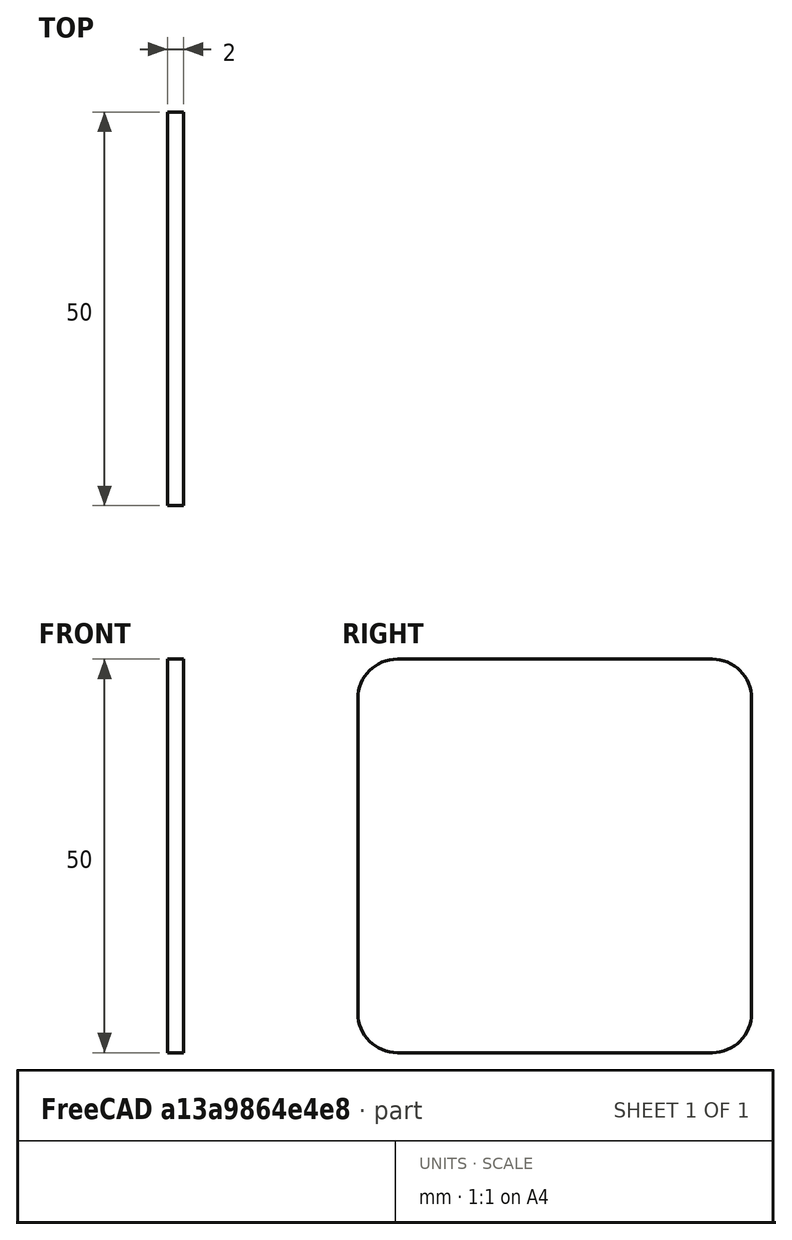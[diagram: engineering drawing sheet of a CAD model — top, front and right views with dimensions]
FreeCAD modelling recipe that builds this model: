
FCSTD DOCUMENT  (FreeCAD 0.20R25352 (Git))
Label: gopro mount
License: All rights reserved
LicenseURL: http://en.wikipedia.org/wiki/All_rights_reserved
objects: Sketcher::SketchObject×2, PartDesign::Pad×1, PartDesign::Body×1
note: 5 computed .brp shape members not serialized (recipe doc carries the construction recipe); baked Part::Feature solids carry a one-line shape summary decoded from their .brp

FEATURE [Sketcher::SketchObject] Sketch003
  FullyConstrained = true
  MapMode = 3
  Placement = pos=(0,0,0) rot=(0.707107,0.707107,0;3.14159rad)
  Support = -> [Sketch003]
  sketch-geometry (5):
    g0: LineSegment StartX=-8 StartY=0 StartZ=0 EndX=8 EndY=0 EndZ=0
    g1: LineSegment StartX=8 StartY=0 StartZ=0 EndX=8 EndY=12 EndZ=0
    g2: LineSegment StartX=-8 StartY=12 StartZ=0 EndX=-8 EndY=0 EndZ=0
    g3: ArcOfCircle CenterX=0 CenterY=12 CenterZ=0 NormalX=0 NormalY=0 NormalZ=1 AngleXU=0 Radius=8 StartAngle=0 EndAngle=3.14159
    g4: Circle CenterX=0 CenterY=12 CenterZ=0 NormalX=0 NormalY=0 NormalZ=1 AngleXU=0 Radius=3
  constraints (14):
    c: Vertical(g2)
    c: Vertical(g1)
    c: Horizontal(g2,g1)
    c: DistanceY(g2,g2) = 12
    c: Coincident(g3,g2)
    c: Coincident(g3,g1)
    c: Coincident(g4,g3)
    c: Diameter(g4) = 6
    c: Horizontal(g0)
    c: Horizontal(g3,g2)
    c: Coincident(g2,g0)
    c: Coincident(g0,g1)
    c: DistanceX(g0,g0) = 16
    c: Symmetric(g0,g0,g-1)
FEATURE [Sketcher::SketchObject] Sketch004
  FullyConstrained = true
  MapMode = 2
  Placement = pos=(-1.65,7e-16,-5e-16) rot=(0.57735,0.57735,-0.57735;4.18879rad)
  Support = -> [Sketch004]
  sketch-geometry (12):
    g0: LineSegment StartX=-20 StartY=25 StartZ=0 EndX=20 EndY=25 EndZ=0
    g1: LineSegment StartX=25 StartY=20 StartZ=0 EndX=25 EndY=-20 EndZ=0
    g2: LineSegment StartX=20 StartY=-25 StartZ=0 EndX=-20 EndY=-25 EndZ=0
    g3: LineSegment StartX=-25 StartY=-20 StartZ=0 EndX=-25 EndY=20 EndZ=0
    g4: ArcOfCircle CenterX=20 CenterY=20 CenterZ=0 NormalX=0 NormalY=0 NormalZ=1 AngleXU=0 Radius=5 StartAngle=0 EndAngle=1.5708
    g5: GeomPoint X=25 Y=25 Z=0
    g6: ArcOfCircle CenterX=20 CenterY=-20 CenterZ=0 NormalX=0 NormalY=0 NormalZ=1 AngleXU=0 Radius=5 StartAngle=4.71239 EndAngle=6.28319
    g7: GeomPoint X=25 Y=-25 Z=0
    g8: ArcOfCircle CenterX=-20 CenterY=-20 CenterZ=0 NormalX=0 NormalY=0 NormalZ=1 AngleXU=0 Radius=5 StartAngle=3.14159 EndAngle=4.71239
    g9: GeomPoint X=-25 Y=-25 Z=0
    g10: ArcOfCircle CenterX=-20 CenterY=20 CenterZ=0 NormalX=0 NormalY=0 NormalZ=1 AngleXU=0 Radius=5 StartAngle=1.5708 EndAngle=3.14159
    g11: GeomPoint X=-25 Y=25 Z=0
  constraints (26):
    c: Horizontal(g2)
    c: Vertical(g1)
    c: Vertical(g3)
    c: Symmetric(g5,g11,g-2)
    c: PointOnObject(g5,g0)
    c: PointOnObject(g5,g1)
    c: Tangent(g0,g4) = 1.5708
    c: Tangent(g1,g4) = 1.5708
    c: PointOnObject(g7,g1)
    c: PointOnObject(g7,g2)
    c: Tangent(g1,g6) = 1.5708
    c: Tangent(g2,g6) = 1.5708
    c: PointOnObject(g9,g2)
    c: PointOnObject(g9,g3)
    c: Tangent(g2,g8) = 1.5708
    c: Tangent(g3,g8) = 1.5708
    c: PointOnObject(g11,g3)
    c: PointOnObject(g11,g0)
    c: Tangent(g3,g10) = 1.5708
    c: Tangent(g0,g10) = 1.5708
    c: Equal(g10,g4)
    c: Equal(g4,g6)
    c: Radius(g10) = 5
    c: Symmetric(g8,g4,g-1)
    c: Equal(g3,g0)
    c: DistanceX(g0,g0) = 40
FEATURE [PartDesign::Pad] Pad
  Direction = (-1,4e-16,-4e-16)
  Length = 2
  Length2 = 100
  Placement = pos=(-1.65,7e-16,-5e-16) rot=(0.57735,0.57735,-0.57735;4.18879rad)
  Profile = -> Sketch004
  Type = 0
FEATURE [PartDesign::Body] Body
  Group = -> [Sketch004,Sketch003,Pad]
  Origin = -> Origin
  Tip = -> Pad
